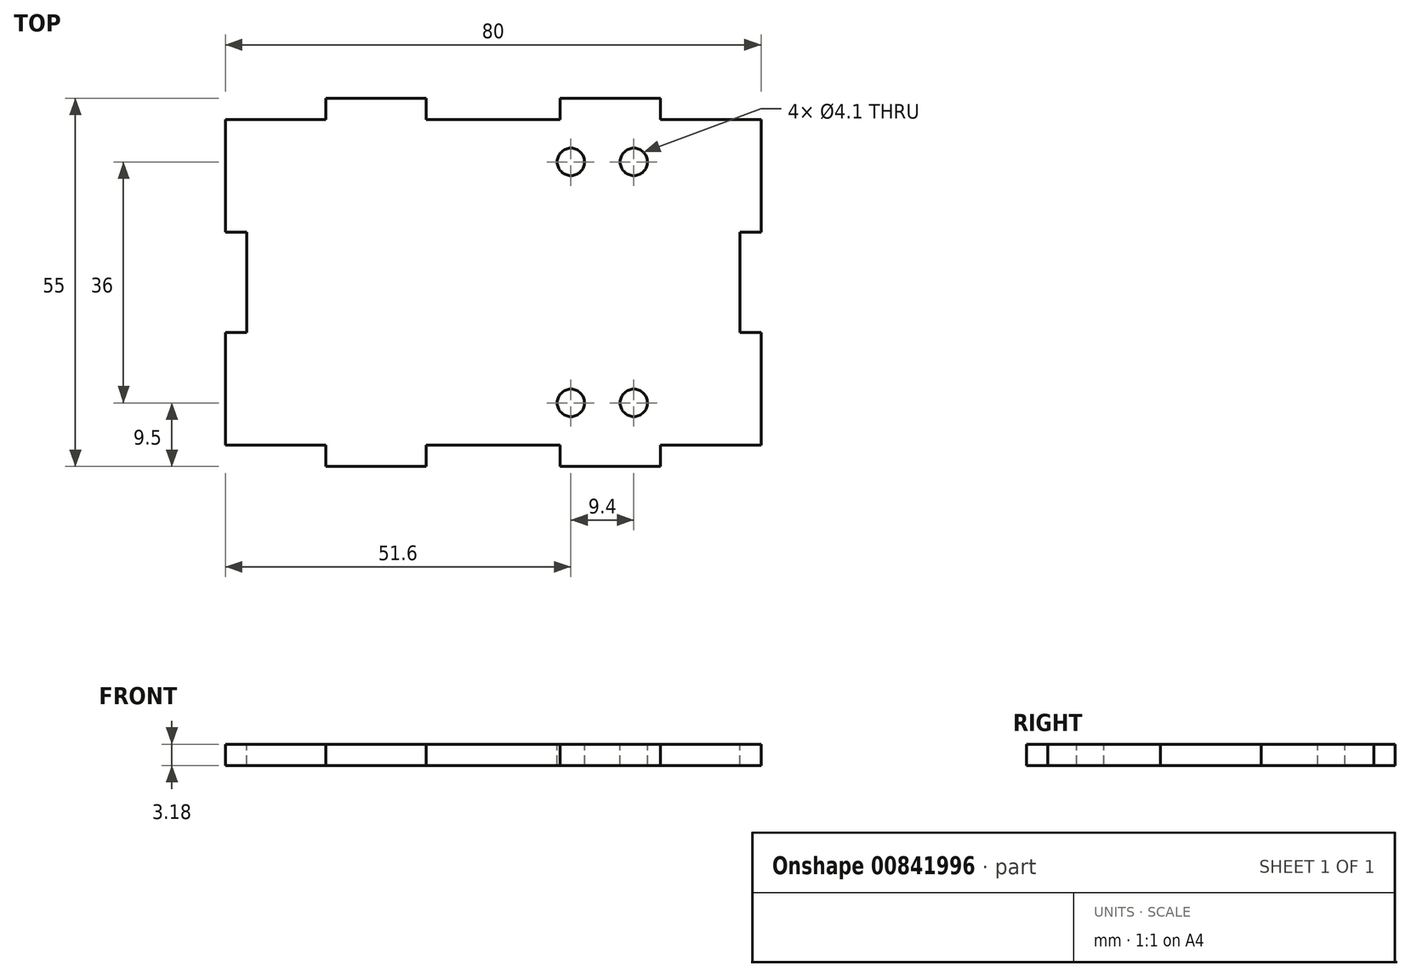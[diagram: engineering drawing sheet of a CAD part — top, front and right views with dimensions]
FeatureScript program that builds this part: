
annotation { "Feature Type Name" : "Feature", "Feature Type Description" : "" }
export const myFeature = defineFeature(function(context is Context, id is Id, definition is map)
    precondition{}
    {
        {
            assignVariable(context, id + "F0", {"name" : "mat_t", "anyValue" : 3.17});
        }
        {
            var Q0;
            Q0=qCreatedBy(makeId("Top.planeOp"),FACE);
            var sketch = newSketch(context, id + "F1", { "sketchPlane" : qUnion([Q0])});
            skLineSegment(sketch, "E0.bottom", {"start": v(40, -24.32) * mm, "end": v(-40, -24.33) * mm});
            skLineSegment(sketch, "E0.top", {"start": v(40, 24.33) * mm, "end": v(-40, 24.32) * mm});
            skLineSegment(sketch, "E0.left", {"start": v(40, -24.32) * mm, "end": v(40, 24.33) * mm});
            skLineSegment(sketch, "E0.right", {"start": v(-40, -24.33) * mm, "end": v(-40, 24.32) * mm});
            skPoint(sketch, "E0.middle", {"position": v(0, 0) * mm});
            skSolve(sketch);
        }
        {
            var Q0;
            Q0 = qSketchRegion(id + "F1", true);
            extrude(context, id + "F2", {"entities" : qUnion([Q0]), "depth" : (getVariable(context, 'mat_t')) * mm, "offsetDistance" : 25 * mm});
        }
        {
            var Q0;
            Q0=makeQuery(id+"F2.opExtrude","CAP_FACE",FACE,{"disambiguationData":[OSD([sQuery(id+"F1.wireOp",EDGE,"E0.bottom"),sQuery(id+"F1.wireOp",EDGE,"E0.top"),sQuery(id+"F1.wireOp",EDGE,"E0.left"),sQuery(id+"F1.wireOp",EDGE,"E0.right")])],"isStart":false});
            var sketch = newSketch(context, id + "F3", { "sketchPlane" : qUnion([Q0])});
            skLineSegment(sketch, "E1.bottom", {"start": v(-25, -24.33) * mm, "end": v(-10, -24.33) * mm});
            skLineSegment(sketch, "E1.top", {"start": v(-25, -27.5) * mm, "end": v(-10, -27.5) * mm});
            skLineSegment(sketch, "E1.left", {"start": v(-25, -24.33) * mm, "end": v(-25, -27.5) * mm});
            skLineSegment(sketch, "E1.right", {"start": v(-10, -24.33) * mm, "end": v(-10, -27.5) * mm});
            skLineSegment(sketch, "E2", {"start": v(0, 24.33) * mm, "end": v(0, -24.33) * mm, "construction": true});
            skLineSegment(sketch, "E3", {"start": v(-40, 0) * mm, "end": v(40, 0) * mm, "construction": true});
            skLineSegment(sketch, "E4.MirrorCS", {"start": v(25, -24.33) * mm, "end": v(25, -27.5) * mm});
            skLineSegment(sketch, "E5.MirrorCS", {"start": v(10, -24.33) * mm, "end": v(10, -27.5) * mm});
            skLineSegment(sketch, "E6.MirrorCS", {"start": v(25, -24.32) * mm, "end": v(10, -24.33) * mm});
            skLineSegment(sketch, "E7.MirrorCS", {"start": v(25, -27.5) * mm, "end": v(10, -27.5) * mm});
            skLineSegment(sketch, "E8.MirrorCS", {"start": v(-25, 24.33) * mm, "end": v(-25, 27.5) * mm});
            skLineSegment(sketch, "E9.MirrorCS", {"start": v(-10, 24.33) * mm, "end": v(-10, 27.5) * mm});
            skLineSegment(sketch, "E10.MirrorCS", {"start": v(10, 24.33) * mm, "end": v(10, 27.5) * mm});
            skLineSegment(sketch, "E11.MirrorCS", {"start": v(25, 24.33) * mm, "end": v(25, 27.5) * mm});
            skLineSegment(sketch, "E12.MirrorCS", {"start": v(25, 27.5) * mm, "end": v(10, 27.5) * mm});
            skLineSegment(sketch, "E13.MirrorCS", {"start": v(25, 24.33) * mm, "end": v(10, 24.33) * mm});
            skLineSegment(sketch, "E14.MirrorCS", {"start": v(-25, 24.32) * mm, "end": v(-10, 24.33) * mm});
            skLineSegment(sketch, "E15.MirrorCS", {"start": v(-25, 27.5) * mm, "end": v(-10, 27.5) * mm});
            skLineSegment(sketch, "E16", {"start": v(-17.5, -24.33) * mm, "end": v(-17.5, -27.5) * mm, "construction": true});
            skLineSegment(sketch, "E17", {"start": v(17.5, -24.33) * mm, "end": v(17.5, -27.5) * mm, "construction": true});
            skSolve(sketch);
        }
        {
            var Q0;
            Q0 = qSketchRegion(id + "F3", true);
            var Q1;
            Q1=makeQuery(id+"F2.opExtrude","CAP_FACE",FACE,{"disambiguationData":[OSD([sQuery(id+"F1.wireOp",EDGE,"E0.bottom"),sQuery(id+"F1.wireOp",EDGE,"E0.top"),sQuery(id+"F1.wireOp",EDGE,"E0.left"),sQuery(id+"F1.wireOp",EDGE,"E0.right")])],"isStart":true});
            extrude(context, id + "F4", {"entities" : qUnion([Q0]), "operationType" : NewBodyOperationType.ADD, "endBound" : BoundingType.UP_TO_SURFACE, "oppositeDirection" : true, "depth" : 25 * mm, "endBoundEntityFace" : qUnion([Q1]), "offsetDistance" : 25 * mm});
        }
        {
            var Q0;
            Q0=makeQuery(id+"F4.boolean.opBoolean","MERGE",FACE,{"derivedFrom":[makeQuery(id+"F2.opExtrude","CAP_FACE",FACE,{"disambiguationData":[OSD([sQuery(id+"F1.wireOp",EDGE,"E0.bottom"),sQuery(id+"F1.wireOp",EDGE,"E0.top"),sQuery(id+"F1.wireOp",EDGE,"E0.left"),sQuery(id+"F1.wireOp",EDGE,"E0.right")])],"isStart":false}),makeQuery(id+"F4.opExtrude","CAP_FACE",FACE,{"disambiguationData":[OSD([sQuery(id+"F3.wireOp",EDGE,"E1.bottom"),sQuery(id+"F3.wireOp",EDGE,"E1.top"),sQuery(id+"F3.wireOp",EDGE,"E1.left"),sQuery(id+"F3.wireOp",EDGE,"E1.right")])],"isStart":true}),makeQuery(id+"F4.opExtrude","CAP_FACE",FACE,{"disambiguationData":[OSD([sQuery(id+"F3.wireOp",EDGE,"E4.MirrorCS"),sQuery(id+"F3.wireOp",EDGE,"E5.MirrorCS"),sQuery(id+"F3.wireOp",EDGE,"E6.MirrorCS"),sQuery(id+"F3.wireOp",EDGE,"E7.MirrorCS")])],"isStart":true}),makeQuery(id+"F4.opExtrude","CAP_FACE",FACE,{"disambiguationData":[OSD([sQuery(id+"F3.wireOp",EDGE,"E8.MirrorCS"),sQuery(id+"F3.wireOp",EDGE,"E9.MirrorCS"),sQuery(id+"F3.wireOp",EDGE,"E14.MirrorCS"),sQuery(id+"F3.wireOp",EDGE,"E15.MirrorCS")])],"isStart":true}),makeQuery(id+"F4.opExtrude","CAP_FACE",FACE,{"disambiguationData":[OSD([sQuery(id+"F3.wireOp",EDGE,"E10.MirrorCS"),sQuery(id+"F3.wireOp",EDGE,"E11.MirrorCS"),sQuery(id+"F3.wireOp",EDGE,"E12.MirrorCS"),sQuery(id+"F3.wireOp",EDGE,"E13.MirrorCS")])],"isStart":true})]});
            var sketch = newSketch(context, id + "F5", { "sketchPlane" : qUnion([Q0])});
            skLineSegment(sketch, "E18", {"start": v(40, 0) * mm, "end": v(-40, 0) * mm, "construction": true});
            skLineSegment(sketch, "E19.bottom", {"start": v(40, 7.5) * mm, "end": v(36.83, 7.5) * mm});
            skLineSegment(sketch, "E19.top", {"start": v(40, -7.5) * mm, "end": v(36.83, -7.5) * mm});
            skLineSegment(sketch, "E19.left", {"start": v(40, 7.5) * mm, "end": v(40, -7.5) * mm});
            skLineSegment(sketch, "E19.right", {"start": v(36.83, 7.5) * mm, "end": v(36.83, -7.5) * mm});
            skLineSegment(sketch, "E20", {"start": v(0, 24.33) * mm, "end": v(0, -24.33) * mm, "construction": true});
            skLineSegment(sketch, "E21.MirrorCS", {"start": v(-40, 7.5) * mm, "end": v(-40, -7.5) * mm});
            skLineSegment(sketch, "E22.MirrorCS", {"start": v(-40, -7.5) * mm, "end": v(-36.82, -7.5) * mm});
            skLineSegment(sketch, "E23.MirrorCS", {"start": v(-36.82, 7.5) * mm, "end": v(-36.82, -7.5) * mm});
            skLineSegment(sketch, "E24.MirrorCS", {"start": v(-40, 7.5) * mm, "end": v(-36.82, 7.5) * mm});
            skSolve(sketch);
        }
        {
            var Q0;
            Q0 = qSketchRegion(id + "F5", true);
            extrude(context, id + "F6", {"entities" : qUnion([Q0]), "operationType" : NewBodyOperationType.REMOVE, "endBound" : BoundingType.THROUGH_ALL, "oppositeDirection" : true, "depth" : 25 * mm, "offsetDistance" : 25 * mm});
        }
        {
            var Q0;
            Q0=makeQuery(id+"F4.boolean.opBoolean","MERGE",FACE,{"derivedFrom":[makeQuery(id+"F2.opExtrude","CAP_FACE",FACE,{"disambiguationData":[OSD([sQuery(id+"F1.wireOp",EDGE,"E0.bottom"),sQuery(id+"F1.wireOp",EDGE,"E0.top"),sQuery(id+"F1.wireOp",EDGE,"E0.left"),sQuery(id+"F1.wireOp",EDGE,"E0.right")])],"isStart":false}),makeQuery(id+"F4.opExtrude","CAP_FACE",FACE,{"disambiguationData":[OSD([sQuery(id+"F3.wireOp",EDGE,"E1.bottom"),sQuery(id+"F3.wireOp",EDGE,"E1.top"),sQuery(id+"F3.wireOp",EDGE,"E1.left"),sQuery(id+"F3.wireOp",EDGE,"E1.right")])],"isStart":true}),makeQuery(id+"F4.opExtrude","CAP_FACE",FACE,{"disambiguationData":[OSD([sQuery(id+"F3.wireOp",EDGE,"E4.MirrorCS"),sQuery(id+"F3.wireOp",EDGE,"E5.MirrorCS"),sQuery(id+"F3.wireOp",EDGE,"E6.MirrorCS"),sQuery(id+"F3.wireOp",EDGE,"E7.MirrorCS")])],"isStart":true}),makeQuery(id+"F4.opExtrude","CAP_FACE",FACE,{"disambiguationData":[OSD([sQuery(id+"F3.wireOp",EDGE,"E8.MirrorCS"),sQuery(id+"F3.wireOp",EDGE,"E9.MirrorCS"),sQuery(id+"F3.wireOp",EDGE,"E14.MirrorCS"),sQuery(id+"F3.wireOp",EDGE,"E15.MirrorCS")])],"isStart":true}),makeQuery(id+"F4.opExtrude","CAP_FACE",FACE,{"disambiguationData":[OSD([sQuery(id+"F3.wireOp",EDGE,"E10.MirrorCS"),sQuery(id+"F3.wireOp",EDGE,"E11.MirrorCS"),sQuery(id+"F3.wireOp",EDGE,"E12.MirrorCS"),sQuery(id+"F3.wireOp",EDGE,"E13.MirrorCS")])],"isStart":true})]});
            var sketch = newSketch(context, id + "F7", { "sketchPlane" : qUnion([Q0])});
            skLineSegment(sketch, "E25", {"start": v(11.6, 18) * mm, "end": v(11.6, -18) * mm, "construction": true});
            skPoint(sketch, "E26", {"position": v(11.6, 0) * mm});
            skLineSegment(sketch, "E27", {"start": v(21, 18) * mm, "end": v(21, -18) * mm, "construction": true});
            skLineSegment(sketch, "E28", {"start": v(36.83, 0) * mm, "end": v(11.6, 0) * mm, "construction": true});
            skPoint(sketch, "E29", {"position": v(21, 0) * mm});
            skCircle(sketch, "E30", {"center": v(11.6, 18) * mm, "radius": 2.05 * mm});
            skCircle(sketch, "E31", {"center": v(21, 18) * mm, "radius": 2.05 * mm});
            skCircle(sketch, "E32", {"center": v(21, -18) * mm, "radius": 2.05 * mm});
            skCircle(sketch, "E33", {"center": v(11.6, -18) * mm, "radius": 2.05 * mm});
            skSolve(sketch);
        }
        {
            var Q0;
            Q0 = qSketchRegion(id + "F7", true);
            extrude(context, id + "F8", {"entities" : qUnion([Q0]), "operationType" : NewBodyOperationType.REMOVE, "endBound" : BoundingType.THROUGH_ALL, "oppositeDirection" : true, "depth" : 25 * mm, "offsetDistance" : 25 * mm});
        }
    });
